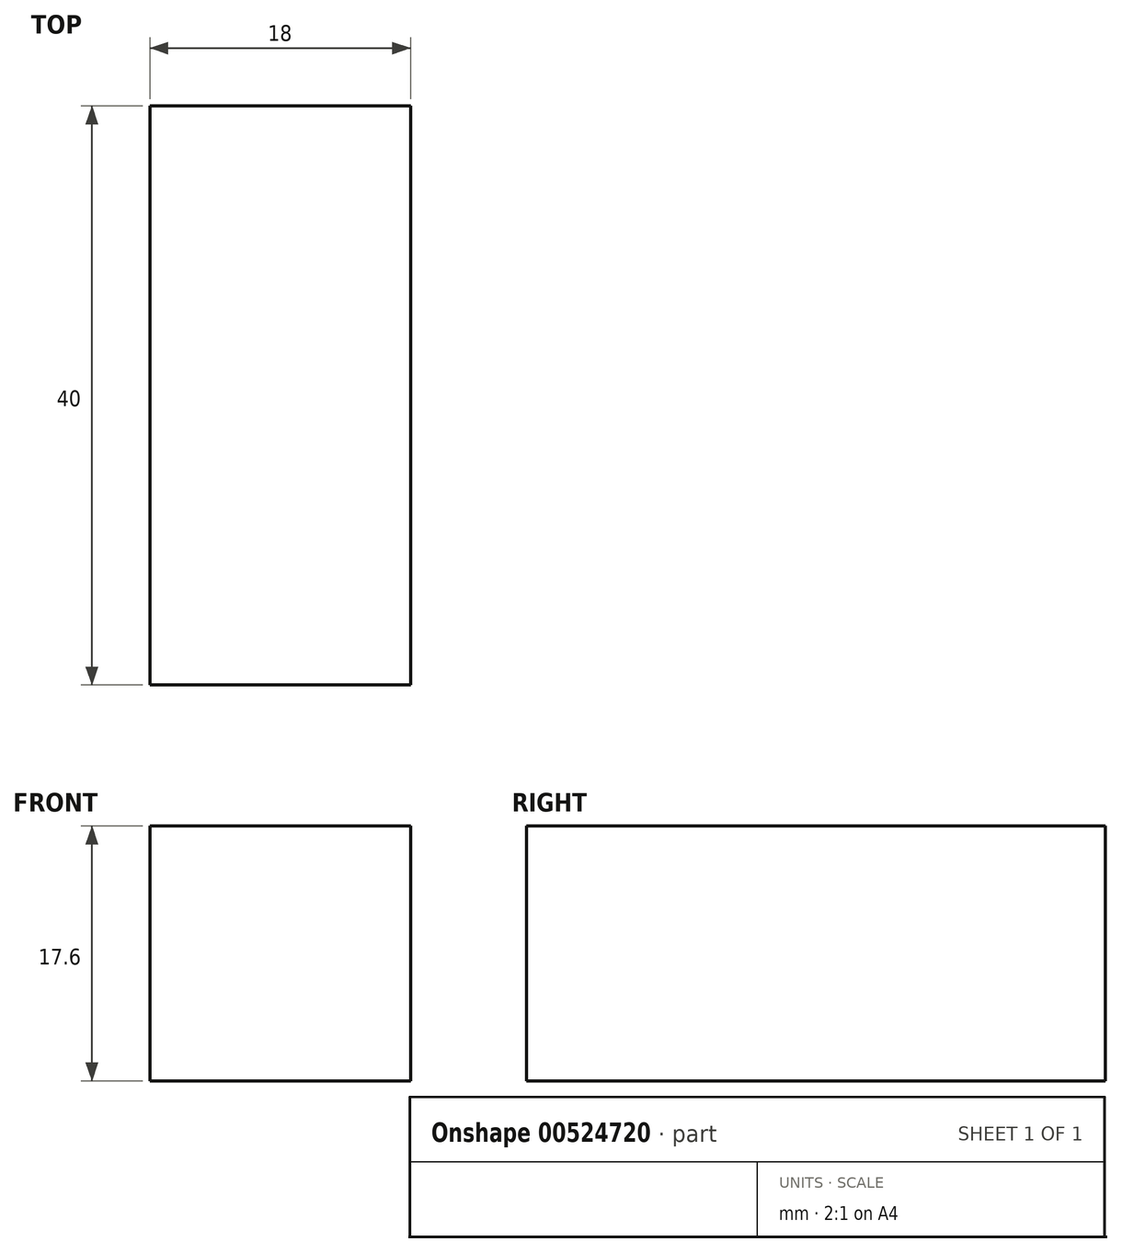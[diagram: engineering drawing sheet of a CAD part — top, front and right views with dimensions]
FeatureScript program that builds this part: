
annotation { "Feature Type Name" : "Feature", "Feature Type Description" : "" }
export const myFeature = defineFeature(function(context is Context, id is Id, definition is map)
    precondition{}
    {
        {
            var Q0;
            Q0=qCreatedBy(makeId("Top.planeOp"),FACE);
            var sketch = newSketch(context, id + "F0", { "sketchPlane" : qUnion([Q0])});
            skLineSegment(sketch, "E0.bottom", {"start": v(9, -20) * mm, "end": v(-9, -20) * mm});
            skLineSegment(sketch, "E0.top", {"start": v(9, 20) * mm, "end": v(-9, 20) * mm});
            skLineSegment(sketch, "E0.left", {"start": v(9, -20) * mm, "end": v(9, 20) * mm});
            skLineSegment(sketch, "E0.right", {"start": v(-9, -20) * mm, "end": v(-9, 20) * mm});
            skPoint(sketch, "E0.middle", {"position": v(0, 0) * mm});
            skSolve(sketch);
        }
        {
            var Q0;
            Q0 = qSketchRegion(id + "F0", true);
            extrude(context, id + "F1", {"entities" : qUnion([Q0]), "depth" : 17.6 * mm, "offsetDistance" : 25 * mm});
        }
    });
